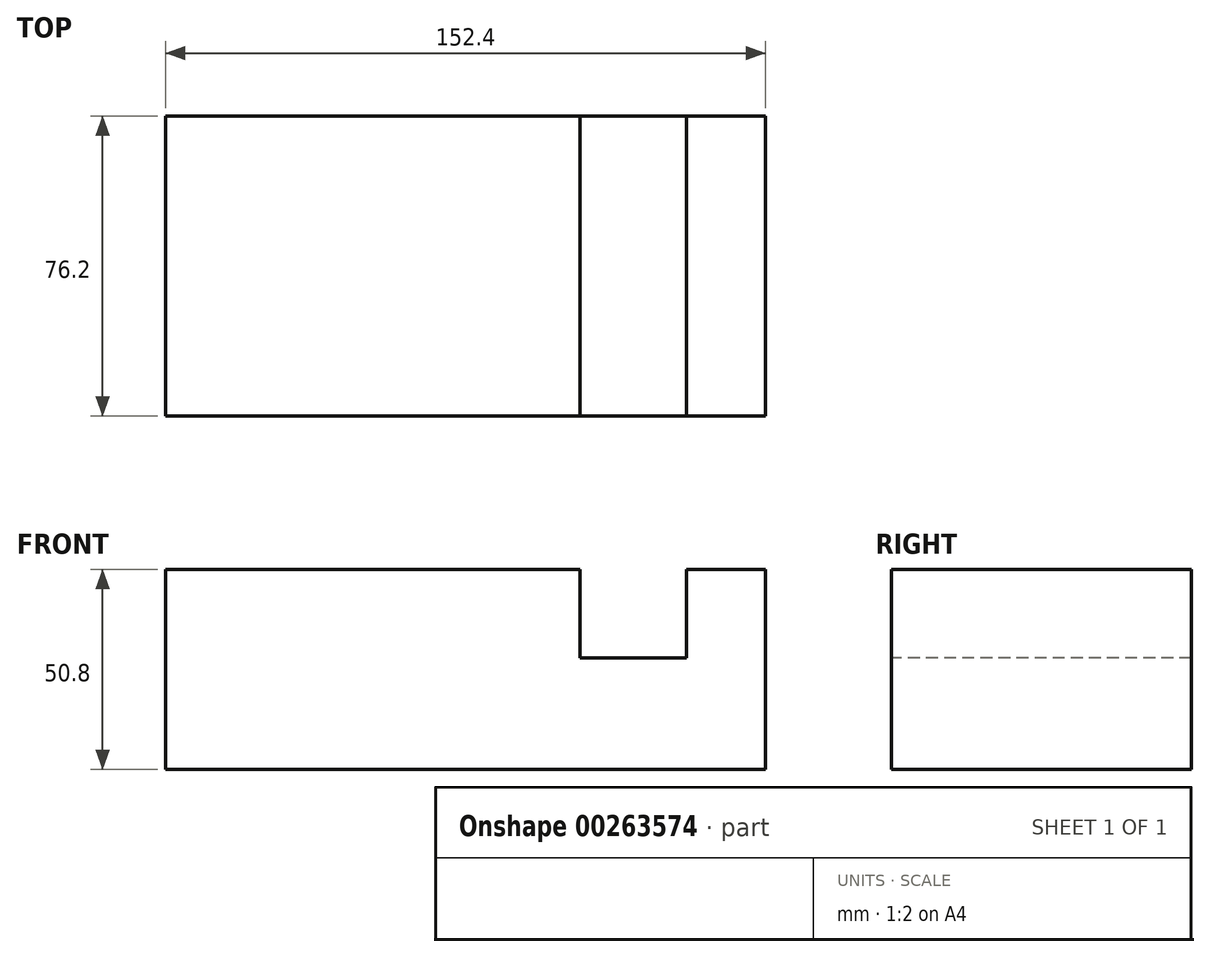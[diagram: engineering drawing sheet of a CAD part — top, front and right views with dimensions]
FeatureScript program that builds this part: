
annotation { "Feature Type Name" : "Feature", "Feature Type Description" : "" }
export const myFeature = defineFeature(function(context is Context, id is Id, definition is map)
    precondition{}
    {
        {
            var Q0;
            Q0=qCreatedBy(makeId("Front.planeOp"),FACE);
            var sketch = newSketch(context, id + "F0", { "sketchPlane" : qUnion([Q0])});
            skLineSegment(sketch, "E0.bottom", {"start": v(-84.4, 22.52) * mm, "end": v(68, 22.52) * mm});
            skLineSegment(sketch, "E0.top", {"start": v(-84.4, -28.28) * mm, "end": v(68, -28.28) * mm});
            skLineSegment(sketch, "E0.left", {"start": v(-84.4, 22.52) * mm, "end": v(-84.4, -28.28) * mm});
            skLineSegment(sketch, "E0.right", {"start": v(68, 22.52) * mm, "end": v(68, -28.28) * mm});
            skSolve(sketch);
        }
        {
            var Q0;
            Q0=makeQuery(id+"F0.imprint","IMPRINT",FACE,{"disambiguationData":[TD([[makeQuery(id+"F0.imprint","IMPRINT",EDGE,{"derivedFrom":sQuery(id+"F0.wireOp",EDGE,"E0.bottom")}),-1.0]])]});
            extrude(context, id + "F1", {"entities" : qUnion([Q0]), "depth" : 76.2 * mm});
        }
        {
            var Q0;
            Q0=makeQuery(id+"F1.opExtrude","CAP_FACE",FACE,{"disambiguationData":[OSD([sQuery(id+"F0.wireOp",EDGE,"E0.bottom"),sQuery(id+"F0.wireOp",EDGE,"E0.top"),sQuery(id+"F0.wireOp",EDGE,"E0.left"),sQuery(id+"F0.wireOp",EDGE,"E0.right")])],"isStart":false});
            var sketch = newSketch(context, id + "F2", { "sketchPlane" : qUnion([Q0])});
            skLineSegment(sketch, "E1", {"start": v(20.94, 22.52) * mm, "end": v(20.94, 0) * mm});
            skLineSegment(sketch, "E2", {"start": v(20.94, 0) * mm, "end": v(48, 0) * mm});
            skLineSegment(sketch, "E3", {"start": v(48, 0) * mm, "end": v(48, 22.52) * mm});
            skLineSegment(sketch, "E4", {"start": v(48, 22.52) * mm, "end": v(20.94, 22.52) * mm});
            skSolve(sketch);
        }
        {
            var Q0;
            Q0 = qSketchRegion(id + "F2", true);
            extrude(context, id + "F3", {"entities" : qUnion([Q0]), "operationType" : NewBodyOperationType.REMOVE, "endBound" : BoundingType.THROUGH_ALL, "oppositeDirection" : true, "depth" : 25.4 * mm});
        }
    });
